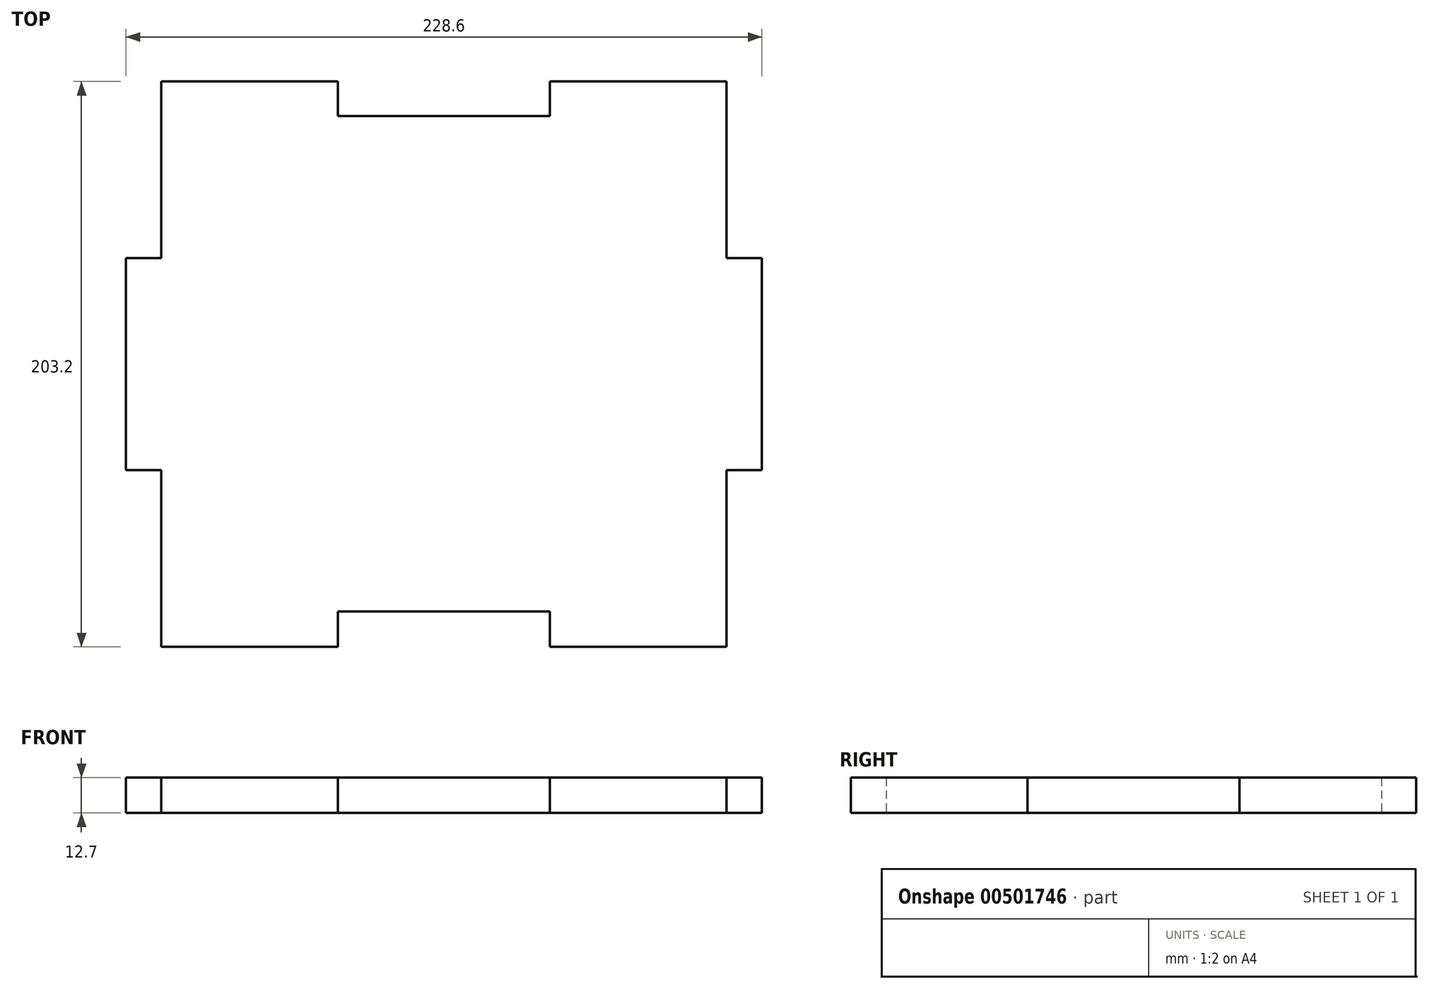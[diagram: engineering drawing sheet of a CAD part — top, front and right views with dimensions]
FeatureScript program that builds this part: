
annotation { "Feature Type Name" : "Feature", "Feature Type Description" : "" }
export const myFeature = defineFeature(function(context is Context, id is Id, definition is map)
    precondition{}
    {
        {
            var Q0;
            Q0=qCreatedBy(makeId("Top.planeOp"),FACE);
            var sketch = newSketch(context, id + "F0", { "sketchPlane" : qUnion([Q0])});
            skLineSegment(sketch, "E0.bottom", {"start": v(-101.6, 101.6) * mm, "end": v(101.6, 101.6) * mm});
            skLineSegment(sketch, "E0.top", {"start": v(-101.6, -101.6) * mm, "end": v(101.6, -101.6) * mm});
            skLineSegment(sketch, "E0.left", {"start": v(-101.6, 101.6) * mm, "end": v(-101.6, -101.6) * mm});
            skLineSegment(sketch, "E0.right", {"start": v(101.6, 101.6) * mm, "end": v(101.6, -101.6) * mm});
            skPoint(sketch, "E0.middle", {"position": v(0, 0) * mm});
            skLineSegment(sketch, "E1.bottom", {"start": v(-38.1, 101.85) * mm, "end": v(38.1, 101.85) * mm});
            skLineSegment(sketch, "E1.top", {"start": v(-38.1, 89.15) * mm, "end": v(38.1, 89.15) * mm});
            skLineSegment(sketch, "E1.left", {"start": v(-38.1, 101.85) * mm, "end": v(-38.1, 89.15) * mm});
            skLineSegment(sketch, "E1.right", {"start": v(38.1, 101.85) * mm, "end": v(38.1, 89.15) * mm});
            skPoint(sketch, "E1.middle", {"position": v(0, 101.6) * mm});
            skLineSegment(sketch, "E2.bottom", {"start": v(-114.3, 38.1) * mm, "end": v(-88.9, 38.1) * mm});
            skLineSegment(sketch, "E2.top", {"start": v(-114.3, -38.1) * mm, "end": v(-88.9, -38.1) * mm});
            skLineSegment(sketch, "E2.left", {"start": v(-114.3, 38.1) * mm, "end": v(-114.3, -38.1) * mm});
            skLineSegment(sketch, "E2.right", {"start": v(-88.9, 38.1) * mm, "end": v(-88.9, -38.1) * mm});
            skPoint(sketch, "E2.middle", {"position": v(-101.6, 0) * mm});
            skLineSegment(sketch, "E3.bottom", {"start": v(-38.1, -88.9) * mm, "end": v(38.1, -88.9) * mm});
            skLineSegment(sketch, "E3.top", {"start": v(-38.1, -101.6) * mm, "end": v(38.1, -101.6) * mm});
            skLineSegment(sketch, "E3.left", {"start": v(-38.1, -88.9) * mm, "end": v(-38.1, -101.6) * mm});
            skLineSegment(sketch, "E3.right", {"start": v(38.1, -88.9) * mm, "end": v(38.1, -101.6) * mm});
            skPoint(sketch, "E3.middle", {"position": v(0, -101.6) * mm});
            skLineSegment(sketch, "E4.bottom", {"start": v(88.9, 38.1) * mm, "end": v(114.3, 38.1) * mm});
            skLineSegment(sketch, "E4.top", {"start": v(88.9, -38.1) * mm, "end": v(114.3, -38.1) * mm});
            skLineSegment(sketch, "E4.left", {"start": v(88.9, 38.1) * mm, "end": v(88.9, -38.1) * mm});
            skLineSegment(sketch, "E4.right", {"start": v(114.3, 38.1) * mm, "end": v(114.3, -38.1) * mm});
            skPoint(sketch, "E4.middle", {"position": v(101.6, 0) * mm});
            skSolve(sketch);
        }
        {
            var Q0;
            {var subQ5=sQuery(id+"F0.wireOp",EDGE,"E2.left");Q0=makeQuery(id+"F0.imprint","IMPRINT",FACE,{"disambiguationData":[TD([[makeQuery(id+"F0.imprint","IMPRINT",EDGE,{"derivedFrom":subQ5}),1.0]])]});}
            var Q1;
            {var subQ5=sQuery(id+"F0.wireOp",EDGE,"E2.right");Q1=makeQuery(id+"F0.imprint","IMPRINT",FACE,{"disambiguationData":[TD([[makeQuery(id+"F0.imprint","IMPRINT",EDGE,{"derivedFrom":subQ5}),-1.0]])]});}
            var Q2;
            {var subQ0=sQuery(id+"F0.wireOp",EDGE,"E1.top");Q2=makeQuery(id+"F0.imprint","IMPRINT",FACE,{"disambiguationData":[TD([[makeQuery(id+"F0.imprint","IMPRINT",EDGE,{"derivedFrom":subQ0}),-1.0]])]});}
            var Q3;
            {var subQ5=sQuery(id+"F0.wireOp",EDGE,"E4.left");Q3=makeQuery(id+"F0.imprint","IMPRINT",FACE,{"disambiguationData":[TD([[makeQuery(id+"F0.imprint","IMPRINT",EDGE,{"derivedFrom":subQ5}),1.0]])]});}
            var Q4;
            {var subQ5=sQuery(id+"F0.wireOp",EDGE,"E4.right");Q4=makeQuery(id+"F0.imprint","IMPRINT",FACE,{"disambiguationData":[TD([[makeQuery(id+"F0.imprint","IMPRINT",EDGE,{"derivedFrom":subQ5}),-1.0]])]});}
            extrude(context, id + "F1", {"entities" : qUnion([Q0, Q1, Q2, Q3, Q4]), "depth" : 12.7 * mm, "offsetDistance" : 25.4 * mm});
        }
    });
